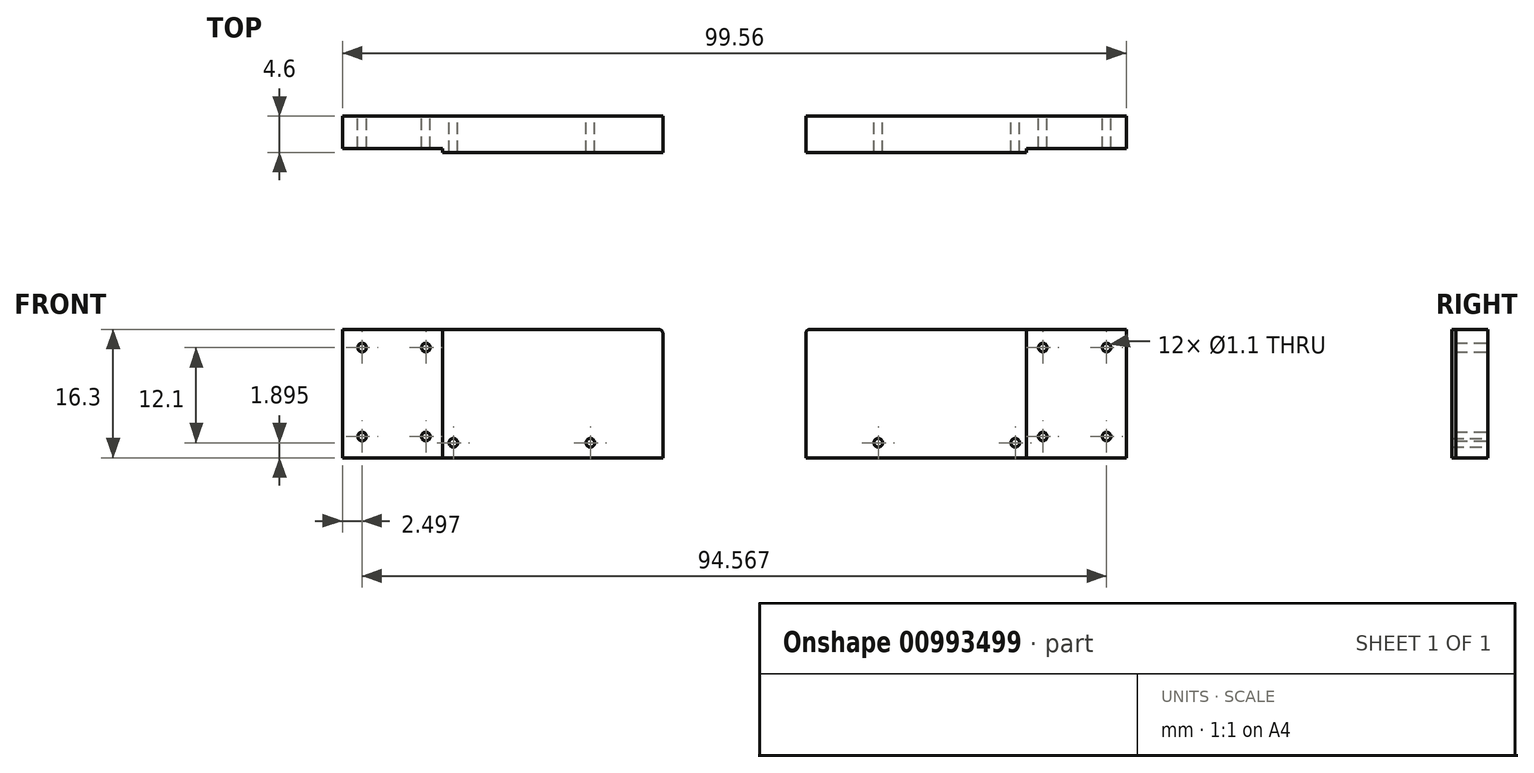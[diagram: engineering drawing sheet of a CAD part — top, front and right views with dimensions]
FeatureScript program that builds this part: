
annotation { "Feature Type Name" : "Feature", "Feature Type Description" : "" }
export const myFeature = defineFeature(function(context is Context, id is Id, definition is map)
    precondition{}
    {
        {
            var Q0;
            Q0=qCreatedBy(makeId("Front.planeOp"),FACE);
            var sketch = newSketch(context, id + "F0", { "sketchPlane" : qUnion([Q0])});
            skLineSegment(sketch, "E0.bottom", {"start": v(-49.78, 34.4) * mm, "end": v(-37.08, 34.4) * mm});
            skLineSegment(sketch, "E0.top", {"start": v(-49.78, 18.1) * mm, "end": v(-37.08, 18.1) * mm});
            skLineSegment(sketch, "E0.left", {"start": v(-49.78, 34.4) * mm, "end": v(-49.78, 18.1) * mm});
            skLineSegment(sketch, "E0.right", {"start": v(-37.08, 34.4) * mm, "end": v(-37.08, 18.1) * mm});
            skLineSegment(sketch, "E1", {"start": v(-37.08, 34.4) * mm, "end": v(-9.08, 34.4) * mm});
            skLineSegment(sketch, "E2", {"start": v(-9.08, 34.4) * mm, "end": v(-9.08, 18.1) * mm});
            skLineSegment(sketch, "E3", {"start": v(-9.08, 18.1) * mm, "end": v(-37.08, 18.1) * mm});
            skPoint(sketch, "E4", {"position": v(-47.28, 32.1) * mm});
            skPoint(sketch, "E5", {"position": v(-39.18, 32.1) * mm});
            skPoint(sketch, "E6", {"position": v(-47.28, 20.8) * mm});
            skPoint(sketch, "E7", {"position": v(-39.18, 20.8) * mm});
            skPoint(sketch, "E8", {"position": v(-35.68, 20) * mm});
            skPoint(sketch, "E9", {"position": v(-18.28, 20) * mm});
            skSolve(sketch);
        }
        {
            var Q0;
            Q0=makeQuery(id+"F0.imprint","IMPRINT",FACE,{"disambiguationData":[TD([[makeQuery(id+"F0.imprint","IMPRINT",EDGE,{"derivedFrom":sQuery(id+"F0.wireOp",EDGE,"E0.right")}),1.0]])]});
            extrude(context, id + "F1", {"entities" : qUnion([Q0]), "depth" : 4.6 * mm, "offsetDistance" : 25 * mm});
        }
        {
            var Q0;
            Q0=makeQuery(id+"F0.imprint","IMPRINT",FACE,{"disambiguationData":[TD([[makeQuery(id+"F0.imprint","IMPRINT",EDGE,{"derivedFrom":sQuery(id+"F0.wireOp",EDGE,"E0.bottom")}),-1.0]])]});
            extrude(context, id + "F2", {"entities" : qUnion([Q0]), "operationType" : NewBodyOperationType.ADD, "depth" : 4.1 * mm, "offsetDistance" : 25 * mm});
        }
        {
            var Q0;
            Q0=sQuery(id+"F0.wireOp",VERTEX,"E5");
            var Q1;
            Q1=sQuery(id+"F0.wireOp",VERTEX,"E4");
            var Q2;
            Q2=sQuery(id+"F0.wireOp",VERTEX,"E6");
            var Q3;
            Q3=sQuery(id+"F0.wireOp",VERTEX,"E7");
            var Q4;
            Q4=sQuery(id+"F0.wireOp",VERTEX,"E8");
            var Q5;
            Q5=sQuery(id+"F0.wireOp",VERTEX,"E9");
            var Q6;
            Q6=makeQuery(id+"F1.opExtrude","SWEPT_BODY",BODY,{"disambiguationData":[OSD([sQuery(id+"F0.wireOp",EDGE,"E0.right"),sQuery(id+"F0.wireOp",EDGE,"E1"),sQuery(id+"F0.wireOp",EDGE,"E2"),sQuery(id+"F0.wireOp",EDGE,"E3")])]});
            hole(context, id + "F3", {"style" : HoleStyle.SIMPLE, "endStyle" : HoleEndStyle.THROUGH, "oppositeDirection" : true, "holeDiameter" : 1.1 * mm, "majorDiameter" : 5 * mm, "isTappedThrough" : true, "tappedDepth" : 12 * mm, "tapClearance" : 3, "locations" : qUnion([Q0, Q1, Q2, Q3, Q4, Q5]), "scope" : qUnion([Q6])});
        }
        {
            var Q0;
            Q0=makeQuery(id+"F1.opExtrude","SWEPT_EDGE",EDGE,{"disambiguationData":[OSD([sQuery(id+"F0.wireOp",EDGE,"E1"),sQuery(id+"F0.wireOp",EDGE,"E2")])]});
            fillet(context, id + "F4", {"entities" : qUnion([Q0]), "radius" : 0.5 * mm, "tangentPropagation" : true, "allowEdgeOverflow" : false});
        }
        {
            var Q0;
            Q0=makeQuery(id+"F1.opExtrude","SWEPT_BODY",BODY,{"disambiguationData":[OSD([sQuery(id+"F0.wireOp",EDGE,"E0.right"),sQuery(id+"F0.wireOp",EDGE,"E1"),sQuery(id+"F0.wireOp",EDGE,"E2"),sQuery(id+"F0.wireOp",EDGE,"E3")])]});
            var Q1;
            Q1=qCreatedBy(makeId("Right.planeOp"),FACE);
            mirror(context, id + "F5", {"entities" : qUnion([Q0]), "mirrorPlane" : qUnion([Q1])});
        }
    });
